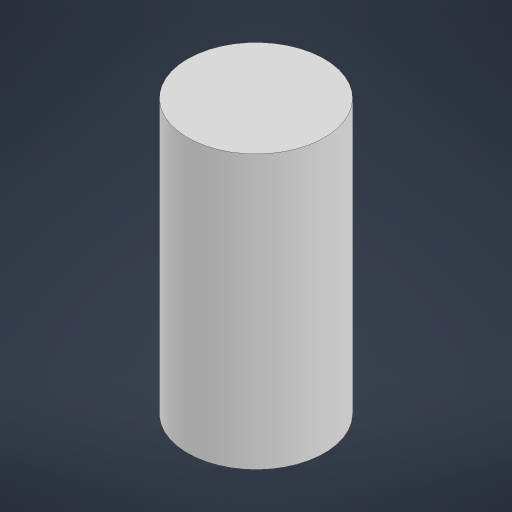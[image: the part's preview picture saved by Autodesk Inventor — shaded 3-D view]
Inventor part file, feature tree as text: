
AUTODESK INVENTOR PART (.ipt)
format: ipt  version: 2023.2 (Build 272271000, 271)  size: 148,480 bytes
history: native  units: mm
features: extrude x1, sketch x1
ambient origin geometry x8: Origin, YZ Plane, XZ Plane, XY Plane, X Axis, Y Axis, Z Axis, Center Point
bodies: Volumenkörper1 (feature_tree)
feature tree (2):
  extrude  "Extrusion1"  Depth=6.0mm TaperAngle=0.0deg
  sketch  "Skizze1"  dims[d0=3.0mm d1=6.0mm d2=0.0mm]
